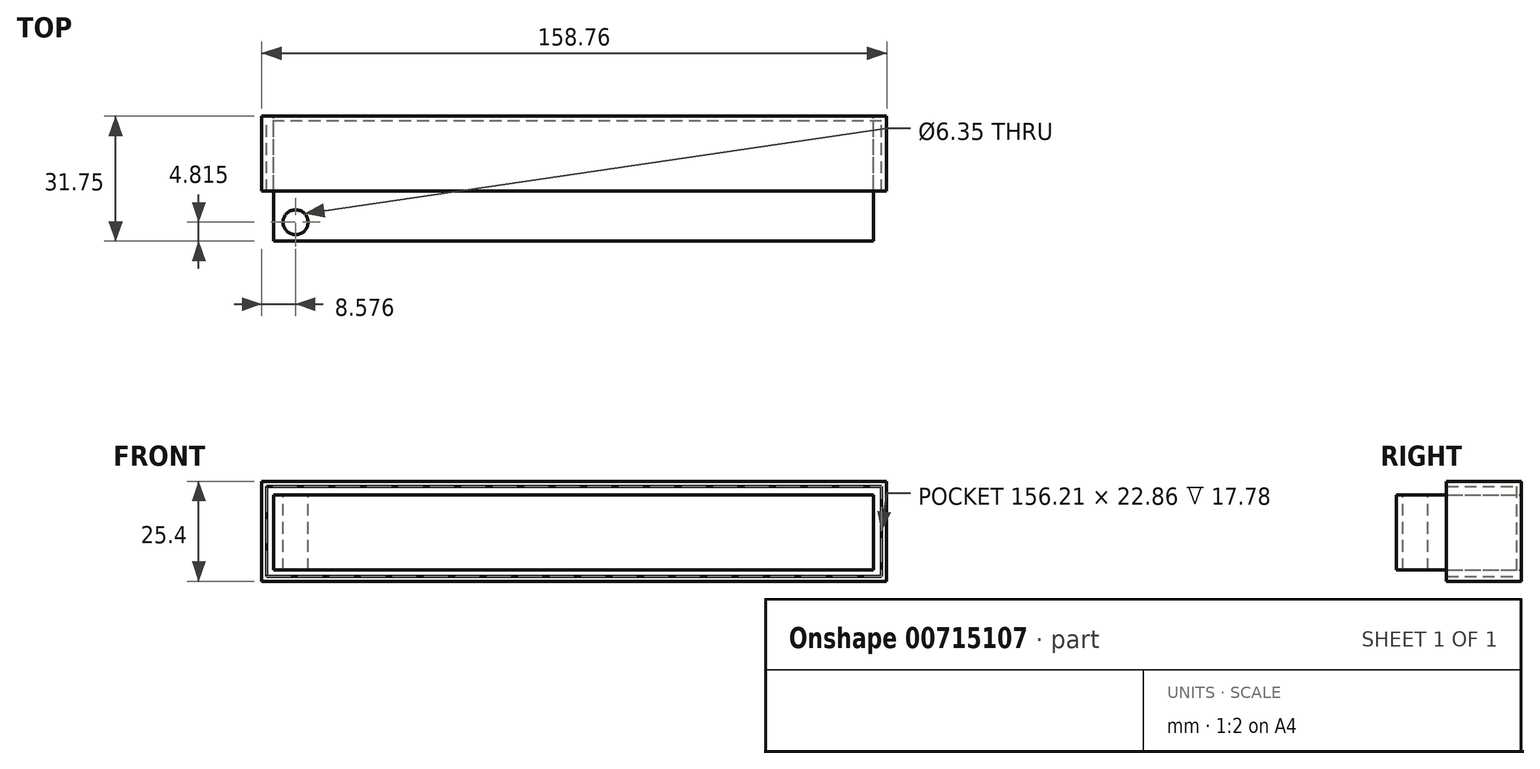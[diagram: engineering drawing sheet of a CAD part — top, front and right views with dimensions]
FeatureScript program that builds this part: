
annotation { "Feature Type Name" : "Feature", "Feature Type Description" : "" }
export const myFeature = defineFeature(function(context is Context, id is Id, definition is map)
    precondition{}
    {
        {
            var Q0;
            Q0=qCreatedBy(makeId("Front.planeOp"),FACE);
            var sketch = newSketch(context, id + "F0", { "sketchPlane" : qUnion([Q0])});
            skLineSegment(sketch, "E0.bottom", {"start": v(79.38, 12.7) * mm, "end": v(-79.38, 12.7) * mm});
            skLineSegment(sketch, "E0.top", {"start": v(79.38, -12.7) * mm, "end": v(-79.38, -12.7) * mm});
            skLineSegment(sketch, "E0.left", {"start": v(79.38, 12.7) * mm, "end": v(79.38, -12.7) * mm});
            skLineSegment(sketch, "E0.right", {"start": v(-79.38, 12.7) * mm, "end": v(-79.38, -12.7) * mm});
            skPoint(sketch, "E0.middle", {"position": v(0, 0) * mm});
            skSolve(sketch);
        }
        {
            var Q0;
            Q0=makeQuery(id+"F0.imprint","IMPRINT",FACE,{"disambiguationData":[TD([[makeQuery(id+"F0.imprint","IMPRINT",EDGE,{"derivedFrom":sQuery(id+"F0.wireOp",EDGE,"E0.bottom")}),1.0]])]});
            extrude(context, id + "F1", {"entities" : qUnion([Q0]), "depth" : 19.05 * mm, "offsetDistance" : 25.4 * mm});
        }
        {
            var Q0;
            Q0=makeQuery(id+"F1.opExtrude","CAP_FACE",FACE,{"disambiguationData":[OSD([sQuery(id+"F0.wireOp",EDGE,"E0.bottom"),sQuery(id+"F0.wireOp",EDGE,"E0.top"),sQuery(id+"F0.wireOp",EDGE,"E0.left"),sQuery(id+"F0.wireOp",EDGE,"E0.right")])],"isStart":false});
            shell(context, id + "F2", {"entities" : qUnion([Q0]), "thickness" : 1.27 * mm});
        }
        {
            var Q0;
            Q0=qCreatedBy(makeId("Front.planeOp"),FACE);
            var sketch = newSketch(context, id + "F3", { "sketchPlane" : qUnion([Q0])});
            skLineSegment(sketch, "E1.bottom", {"start": v(-76.34, -9.83) * mm, "end": v(76.06, -9.83) * mm});
            skLineSegment(sketch, "E1.top", {"start": v(-76.34, 9.22) * mm, "end": v(76.06, 9.22) * mm});
            skLineSegment(sketch, "E1.left", {"start": v(-76.34, -9.83) * mm, "end": v(-76.34, 9.22) * mm});
            skLineSegment(sketch, "E1.right", {"start": v(76.06, -9.83) * mm, "end": v(76.06, 9.22) * mm});
            skSolve(sketch);
        }
        {
            var Q0;
            Q0=makeQuery(id+"F3.imprint","IMPRINT",FACE,{"disambiguationData":[TD([[makeQuery(id+"F3.imprint","IMPRINT",EDGE,{"derivedFrom":sQuery(id+"F3.wireOp",EDGE,"E1.bottom")}),1.0]])]});
            extrude(context, id + "F4", {"entities" : qUnion([Q0]), "depth" : 31.75 * mm, "offsetDistance" : 25.4 * mm});
        }
        {
            var Q0;
            Q0=makeQuery(id+"F4.opExtrude","SWEPT_FACE",FACE,{"disambiguationData":[OSD([sQuery(id+"F3.wireOp",EDGE,"E1.top")])]});
            var sketch = newSketch(context, id + "F5", { "sketchPlane" : qUnion([Q0])});
            skCircle(sketch, "E2", {"center": v(-70.8, -26.94) * mm, "radius": 3.18 * mm});
            skSolve(sketch);
        }
        {
            var Q0;
            Q0=makeQuery(id+"F5.imprint","IMPRINT",FACE,{"disambiguationData":[TD([[makeQuery(id+"F5.imprint","IMPRINT",EDGE,{"derivedFrom":sQuery(id+"F5.wireOp",EDGE,"E2")}),1.0]])]});
            extrude(context, id + "F6", {"entities" : qUnion([Q0]), "operationType" : NewBodyOperationType.REMOVE, "oppositeDirection" : true, "depth" : 25.4 * mm, "offsetDistance" : 25.4 * mm});
        }
    });
